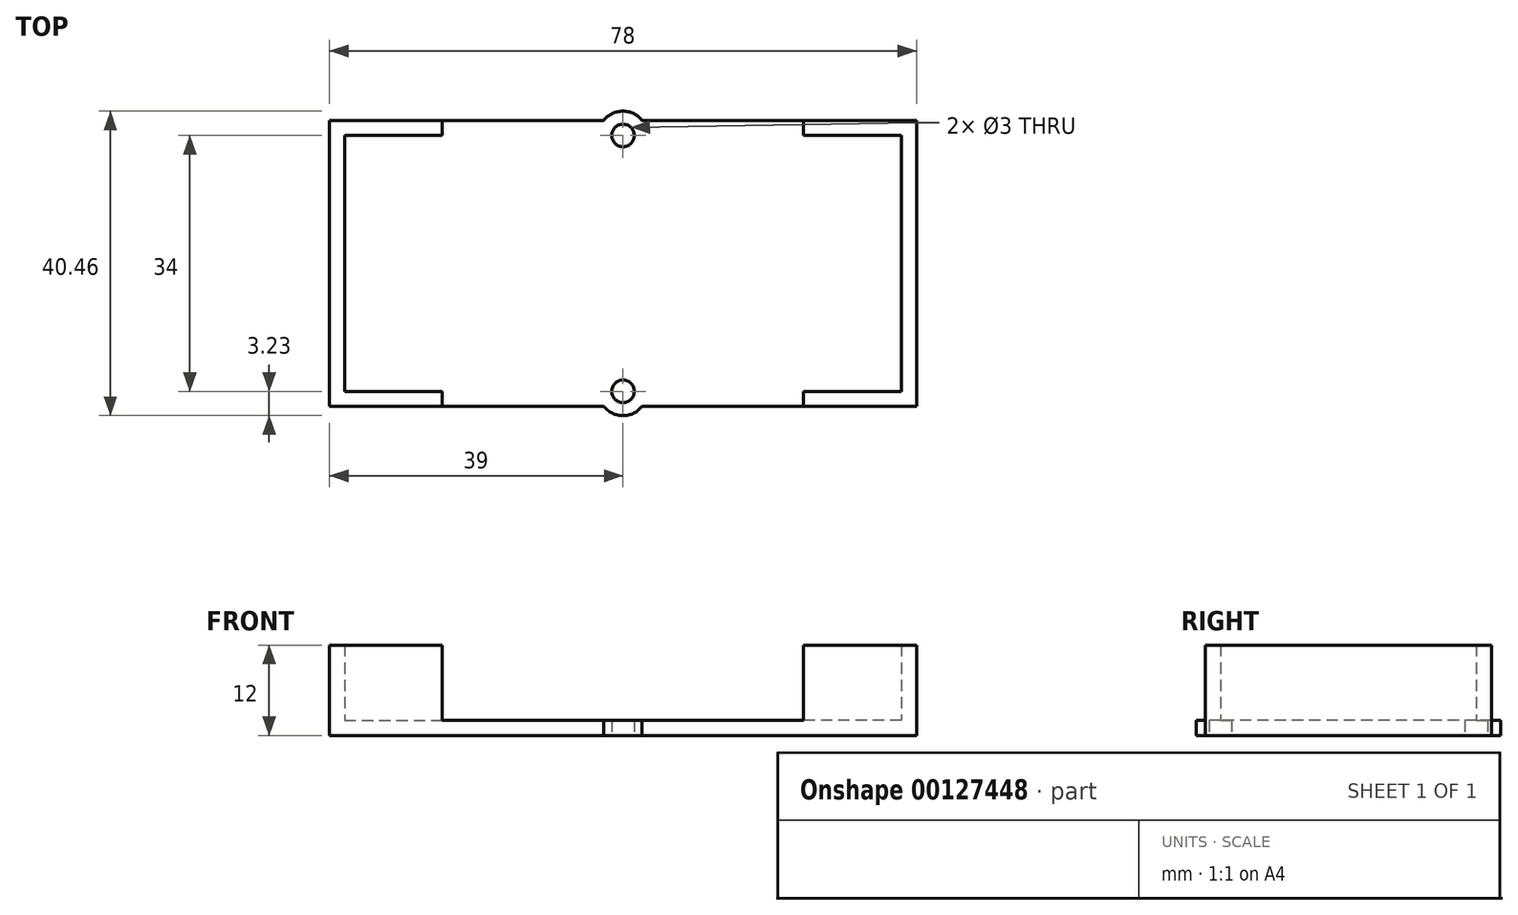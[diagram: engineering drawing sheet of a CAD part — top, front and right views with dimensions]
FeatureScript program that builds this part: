
annotation { "Feature Type Name" : "Feature", "Feature Type Description" : "" }
export const myFeature = defineFeature(function(context is Context, id is Id, definition is map)
    precondition{}
    {
        {
            var Q0;
            Q0=qCreatedBy(makeId("Top.planeOp"),FACE);
            var sketch = newSketch(context, id + "F0", { "sketchPlane" : qUnion([Q0])});
            skLineSegment(sketch, "E0.bottom", {"start": v(0, 0) * mm, "end": v(78, 0) * mm});
            skLineSegment(sketch, "E0.top", {"start": v(0, 38) * mm, "end": v(78, 38) * mm});
            skLineSegment(sketch, "E0.left", {"start": v(0, 0) * mm, "end": v(0, 38) * mm});
            skLineSegment(sketch, "E0.right", {"start": v(78, 0) * mm, "end": v(78, 38) * mm});
            skLineSegment(sketch, "E1", {"start": v(39, 38) * mm, "end": v(39, 0) * mm});
            skCircle(sketch, "E2", {"center": v(39, 36) * mm, "radius": 3.23 * mm});
            skCircle(sketch, "E3", {"center": v(39, 2) * mm, "radius": 3.23 * mm});
            skSolve(sketch);
        }
        {
            var Q0;
            Q0 = qSketchRegion(id + "F0", true);
            extrude(context, id + "F1", {"entities" : qUnion([Q0]), "depth" : 2 * mm});
        }
        {
            var Q0;
            Q0=makeQuery(id+"F1.opExtrude","CAP_FACE",FACE,{"disambiguationData":[OSD([sQuery(id+"F0.wireOp",EDGE,"E0.bottom"),sQuery(id+"F0.wireOp",EDGE,"E0.top"),sQuery(id+"F0.wireOp",EDGE,"E0.left"),sQuery(id+"F0.wireOp",EDGE,"E0.right")])],"isStart":false});
            var sketch = newSketch(context, id + "F2", { "sketchPlane" : qUnion([Q0])});
            skLineSegment(sketch, "E4", {"start": v(15, 36) * mm, "end": v(15, 38) * mm});
            skLineSegment(sketch, "E5", {"start": v(15, 38) * mm, "end": v(0, 38) * mm});
            skLineSegment(sketch, "E6", {"start": v(0, 38) * mm, "end": v(0, 0) * mm});
            skLineSegment(sketch, "E7", {"start": v(0, 0) * mm, "end": v(15, 0) * mm});
            skLineSegment(sketch, "E8", {"start": v(15, 0) * mm, "end": v(15, 2) * mm});
            skLineSegment(sketch, "E9", {"start": v(15, 2) * mm, "end": v(2, 2) * mm});
            skLineSegment(sketch, "E10", {"start": v(2, 2) * mm, "end": v(2, 36) * mm});
            skLineSegment(sketch, "E11", {"start": v(2, 36) * mm, "end": v(15, 36) * mm});
            skLineSegment(sketch, "E12", {"start": v(63, 38) * mm, "end": v(63, 36) * mm});
            skLineSegment(sketch, "E13", {"start": v(63, 36) * mm, "end": v(76, 36) * mm});
            skLineSegment(sketch, "E14", {"start": v(76, 36) * mm, "end": v(76, 2) * mm});
            skLineSegment(sketch, "E15", {"start": v(76, 2) * mm, "end": v(63, 2) * mm});
            skLineSegment(sketch, "E16", {"start": v(63, 2) * mm, "end": v(63, 0) * mm});
            skLineSegment(sketch, "E17", {"start": v(63, 0) * mm, "end": v(78, 0) * mm});
            skLineSegment(sketch, "E18", {"start": v(78, 0) * mm, "end": v(78, 38) * mm});
            skLineSegment(sketch, "E19", {"start": v(78, 38) * mm, "end": v(63, 38) * mm});
            skSolve(sketch);
        }
        {
            var Q0;
            Q0 = qSketchRegion(id + "F2", true);
            extrude(context, id + "F3", {"entities" : qUnion([Q0]), "operationType" : NewBodyOperationType.ADD, "depth" : 10 * mm});
        }
        {
            var Q0;
            Q0=makeQuery(id+"F1.opExtrude","CAP_FACE",FACE,{"disambiguationData":[OSD([sQuery(id+"F0.wireOp",EDGE,"E0.bottom"),sQuery(id+"F0.wireOp",EDGE,"E0.top"),sQuery(id+"F0.wireOp",EDGE,"E0.left"),sQuery(id+"F0.wireOp",EDGE,"E0.right")])],"isStart":true});
            var sketch = newSketch(context, id + "F4", { "sketchPlane" : qUnion([Q0])});
            skLineSegment(sketch, "E20", {"start": v(39, 0) * mm, "end": v(39, -38) * mm});
            skPoint(sketch, "E21", {"position": v(39, -36) * mm});
            skPoint(sketch, "E22", {"position": v(39, -2) * mm});
            skSolve(sketch);
        }
        {
            var Q0;
            Q0=sQuery(id+"F4.wireOp",VERTEX,"E22");
            var Q1;
            Q1=sQuery(id+"F4.wireOp",VERTEX,"E21");
            var Q2;
            Q2=makeQuery(id+"F1.opExtrude","SWEPT_BODY",BODY,{"disambiguationData":[OSD([sQuery(id+"F0.wireOp",EDGE,"E0.bottom"),sQuery(id+"F0.wireOp",EDGE,"E0.top"),sQuery(id+"F0.wireOp",EDGE,"E0.left"),sQuery(id+"F0.wireOp",EDGE,"E0.right")])]});
            hole(context, id + "F5", {"style" : HoleStyle.SIMPLE, "endStyle" : HoleEndStyle.THROUGH, "holeDiameter" : 3 * mm, "locations" : qUnion([Q0, Q1]), "scope" : qUnion([Q2]), "isTappedThrough" : true});
        }
    });
